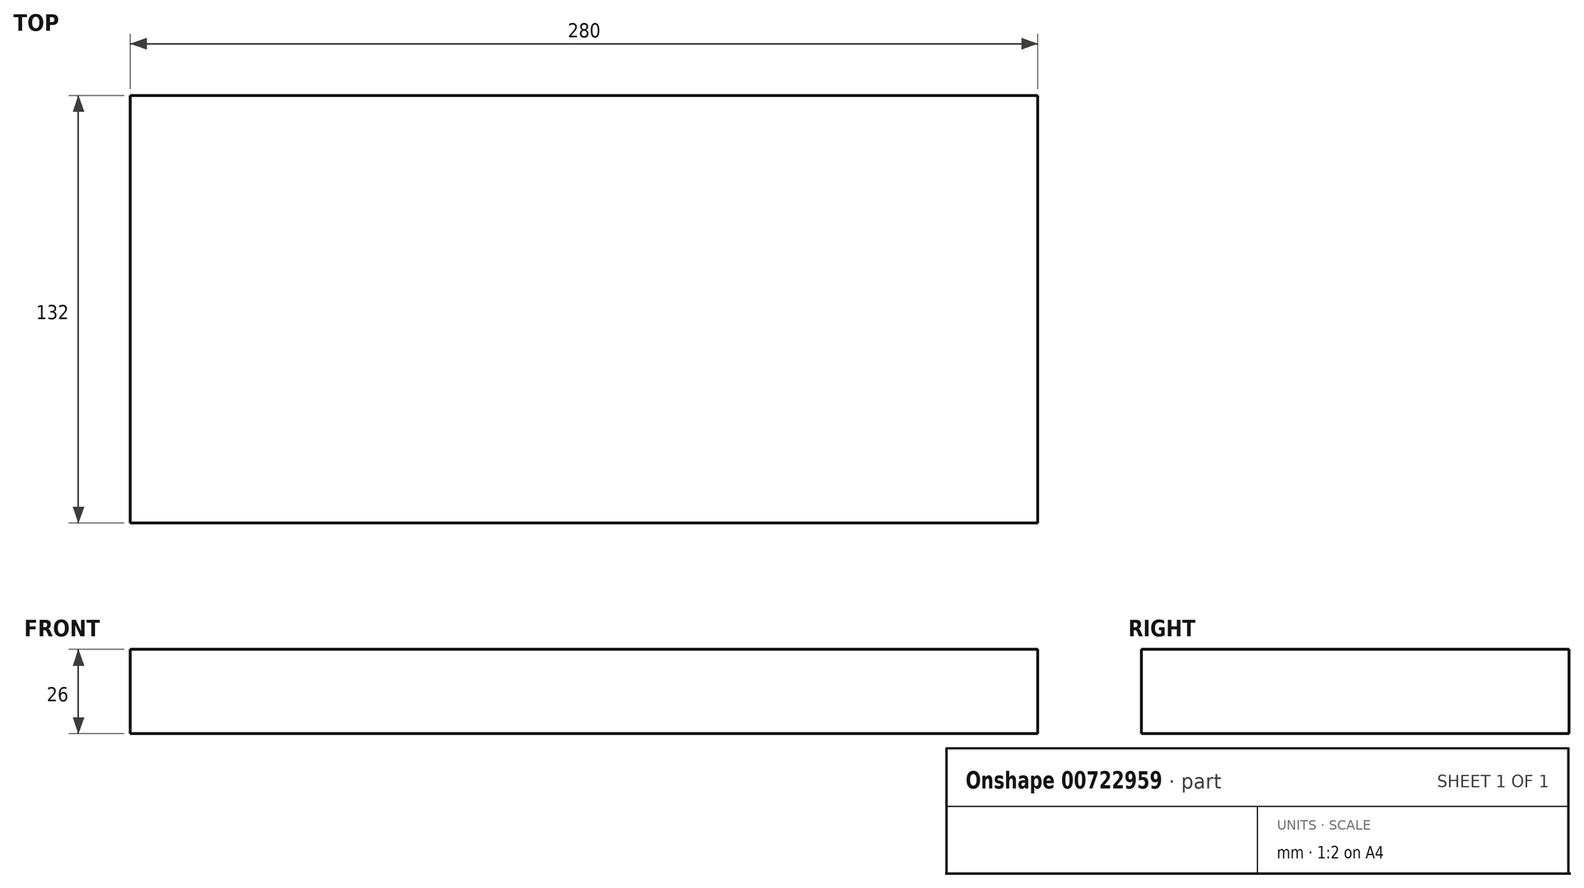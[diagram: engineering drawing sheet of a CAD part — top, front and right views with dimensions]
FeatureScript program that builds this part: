
annotation { "Feature Type Name" : "Feature", "Feature Type Description" : "" }
export const myFeature = defineFeature(function(context is Context, id is Id, definition is map)
    precondition{}
    {
        {
            var Q0;
            Q0=qCreatedBy(makeId("Top.planeOp"),FACE);
            var sketch = newSketch(context, id + "F0", { "sketchPlane" : qUnion([Q0])});
            skLineSegment(sketch, "E0.bottom", {"start": v(-140, 66) * mm, "end": v(140, 66) * mm});
            skLineSegment(sketch, "E0.top", {"start": v(-140, -66) * mm, "end": v(140, -66) * mm});
            skLineSegment(sketch, "E0.left", {"start": v(-140, 66) * mm, "end": v(-140, -66) * mm});
            skLineSegment(sketch, "E0.right", {"start": v(140, 66) * mm, "end": v(140, -66) * mm});
            skLineSegment(sketch, "E1", {"start": v(-140, 66) * mm, "end": v(140, -66) * mm, "construction": true});
            skLineSegment(sketch, "E2", {"start": v(140, 66) * mm, "end": v(-140, -66) * mm, "construction": true});
            skSolve(sketch);
        }
        {
            var Q0;
            Q0 = qSketchRegion(id + "F0", true);
            extrude(context, id + "F1", {"entities" : qUnion([Q0]), "depth" : 26 * mm, "offsetDistance" : 25 * mm});
        }
    });
